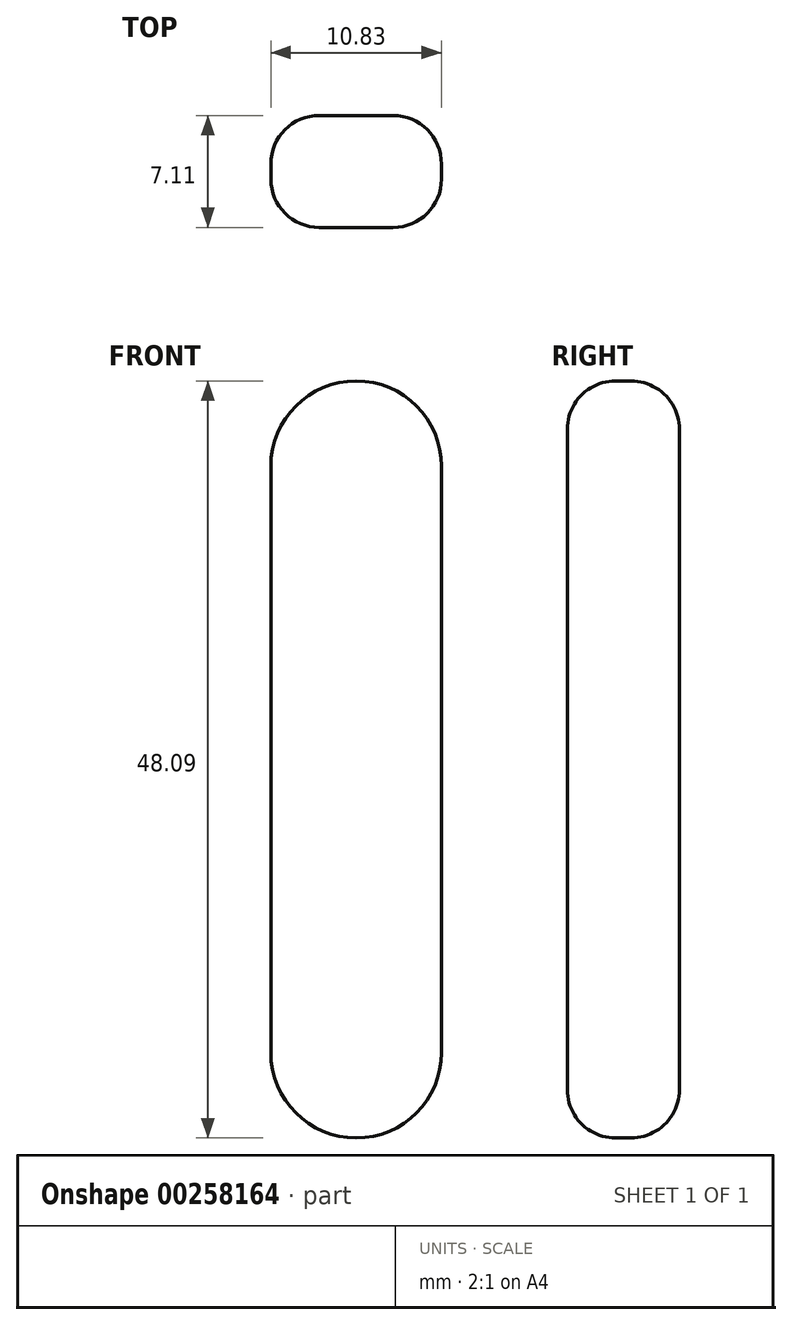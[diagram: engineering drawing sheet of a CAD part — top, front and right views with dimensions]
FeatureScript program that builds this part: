
annotation { "Feature Type Name" : "Feature", "Feature Type Description" : "" }
export const myFeature = defineFeature(function(context is Context, id is Id, definition is map)
    precondition{}
    {
        {
            var Q0;
            Q0=qCreatedBy(makeId("Front.planeOp"),FACE);
            var sketch = newSketch(context, id + "F0", { "sketchPlane" : qUnion([Q0])});
            skLineSegment(sketch, "E0", {"start": v(-5.83, -27.97) * mm, "end": v(-5.83, -2.09) * mm});
            skLineSegment(sketch, "E1", {"start": v(5, -27.97) * mm, "end": v(5, -9.07) * mm});
            skLineSegment(sketch, "E2", {"start": v(5, -9.07) * mm, "end": v(5, -2.09) * mm});
            skArc(sketch, "E3", {"start": v(5, -2.09) * mm, "mid": v(-0.41, 3.33) * mm, "end": v(-5.83, -2.09) * mm});
            skArc(sketch, "E4", {"start": v(-5.83, -2.09) * mm, "mid": v(-0.41, -7.5) * mm, "end": v(5, -2.09) * mm});
            skLineSegment(sketch, "E5", {"start": v(-5.83, -2.09) * mm, "end": v(5, -2.09) * mm});
            skLineSegment(sketch, "E6", {"start": v(5, -2.09) * mm, "end": v(5, 9.28) * mm});
            skLineSegment(sketch, "E7", {"start": v(-5.83, 5.07) * mm, "end": v(-5.83, 9.28) * mm});
            skArc(sketch, "E8", {"start": v(-5.83, 9.28) * mm, "mid": v(-0.41, 14.7) * mm, "end": v(5, 9.28) * mm});
            skLineSegment(sketch, "E9", {"start": v(5, -2.09) * mm, "end": v(5, 1.1) * mm});
            skLineSegment(sketch, "E10", {"start": v(-5.83, 5.07) * mm, "end": v(-5.83, -2.09) * mm});
            skArc(sketch, "E11", {"start": v(-5.83, -27.97) * mm, "mid": v(-0.41, -33.39) * mm, "end": v(5, -27.97) * mm});
            skSolve(sketch);
        }
        {
            var Q0;
            Q0=makeQuery(id+"F0.imprint","IMPRINT",FACE,{"disambiguationData":[TD([[makeQuery(id+"F0.imprint","IMPRINT",EDGE,{"derivedFrom":sQuery(id+"F0.wireOp",EDGE,"E3")}),-1.0]])]});
            var Q1;
            Q1=makeQuery(id+"F0.imprint","IMPRINT",FACE,{"disambiguationData":[TD([[makeQuery(id+"F0.imprint","IMPRINT",EDGE,{"derivedFrom":sQuery(id+"F0.wireOp",EDGE,"E4")}),1.0]])]});
            var Q2;
            Q2=makeQuery(id+"F0.imprint","IMPRINT",FACE,{"disambiguationData":[TD([[makeQuery(id+"F0.imprint","IMPRINT",EDGE,{"derivedFrom":sQuery(id+"F0.wireOp",EDGE,"E3")}),1.0]])]});
            var Q3;
            Q3=makeQuery(id+"F0.imprint","IMPRINT",FACE,{"disambiguationData":[TD([[makeQuery(id+"F0.imprint","IMPRINT",EDGE,{"derivedFrom":sQuery(id+"F0.wireOp",EDGE,"E0")}),-1.0]])]});
            extrude(context, id + "F1", {"entities" : qUnion([Q0, Q1, Q2, Q3]), "depth" : 7.11 * mm});
        }
        {
            var Q0;
            Q0=makeQuery(id+"F1.opExtrude","CAP_EDGE",EDGE,{"disambiguationData":[OSD([sQuery(id+"F0.wireOp",EDGE,"E1"),sQuery(id+"F0.wireOp",EDGE,"E2"),sQuery(id+"F0.wireOp",EDGE,"E6"),sQuery(id+"F0.wireOp",EDGE,"E9")])],"isStart":false});
            var Q1;
            Q1=makeQuery(id+"F1.opExtrude","CAP_EDGE",EDGE,{"disambiguationData":[OSD([sQuery(id+"F0.wireOp",EDGE,"E1"),sQuery(id+"F0.wireOp",EDGE,"E2"),sQuery(id+"F0.wireOp",EDGE,"E6"),sQuery(id+"F0.wireOp",EDGE,"E9")])],"isStart":true});
            var Q2;
            Q2=makeQuery(id+"F1.opExtrude","CAP_EDGE",EDGE,{"disambiguationData":[OSD([sQuery(id+"F0.wireOp",EDGE,"E8")])],"isStart":false});
            var Q3;
            Q3=makeQuery(id+"F1.opExtrude","CAP_EDGE",EDGE,{"disambiguationData":[OSD([sQuery(id+"F0.wireOp",EDGE,"E8")])],"isStart":true});
            var Q4;
            Q4=makeQuery(id+"F1.opExtrude","CAP_EDGE",EDGE,{"disambiguationData":[OSD([sQuery(id+"F0.wireOp",EDGE,"E11")])],"isStart":true});
            var Q5;
            Q5=makeQuery(id+"F1.opExtrude","CAP_EDGE",EDGE,{"disambiguationData":[OSD([sQuery(id+"F0.wireOp",EDGE,"E11")])],"isStart":false});
            var Q6;
            Q6=makeQuery(id+"F1.opExtrude","CAP_EDGE",EDGE,{"disambiguationData":[OSD([sQuery(id+"F0.wireOp",EDGE,"E0"),sQuery(id+"F0.wireOp",EDGE,"E7"),sQuery(id+"F0.wireOp",EDGE,"E10")])],"isStart":true});
            var Q7;
            Q7=makeQuery(id+"F1.opExtrude","CAP_EDGE",EDGE,{"disambiguationData":[OSD([sQuery(id+"F0.wireOp",EDGE,"E0"),sQuery(id+"F0.wireOp",EDGE,"E7"),sQuery(id+"F0.wireOp",EDGE,"E10")])],"isStart":false});
            fillet(context, id + "F2", {"entities" : qUnion([Q0, Q1, Q2, Q3, Q4, Q5, Q6, Q7]), "radius" : 3.07 * mm, "tangentPropagation" : true, "allowEdgeOverflow" : false});
        }
    });
